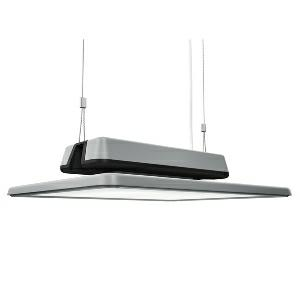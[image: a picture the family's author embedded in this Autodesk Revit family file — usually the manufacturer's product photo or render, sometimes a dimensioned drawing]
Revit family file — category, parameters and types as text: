
# Revit family: acaneo_-_hial_20000_840_w_dali_00734216_865c
name_source: partatom
category: Lighting Fixtures
units: mm (PartAtom-declared; Revit-internal decimal feet)

## family parameters
Cut with Voids When Loaded = No
Host = Face
Light Source = No
Part Type = Normal
Room Calculation Point = No
Round Connector Dimension = Use Diameter
Shared = No

## types (1)
- ACANEO - HIAL 20000/840/W/DALI (1 x LED, 22000 lm, 4000K)
    Apparent Load = 140 VA
    Approval mark = CE
    CIE Flux Codes = 76 97 99 100 100
    Color Rendering = 80-89
    Color Temperature = 4000K
    Control Gear = Electronic ballast
    Default Elevation = 1800 mm
    Description = HIAL 20000/840/W/DALI|High bay luminaire|light source: LED|work equipment: Adjustable electronic ballast, digital DALI|connected load: 220-240 V, 50/60 Hz|Power consumption: approx. 140 W|power factor: approx. 0,951|luminous flux: 22000 lm|luminous efficacy: 157 lm/W|colour temperature: Cold white, ca. 4000 K|color rendering index (CRI): >= 80|chromaticity tolerance:  3 SDCM|System of protection: IP 65|class of protection: I|technology: Continuously dimmable|luminaire body|material: Aluminium|surface: Powder coatet|colour: White aluminium|lamp cover: Acrylic (PMMA), Clear|weight (net): approx. 8.2 kg|mains lead: Built-in plug RST 20i5 Einbau|Fastening: Available separately|Accessory: Junction box (RST 20i5)|minimum ambient temperature: -30 ░C|maximum ambient temperature: 70 ░C|glare control: Optics|unified glare rating(4H 8H): <=  25|
    Frequency = 50 Hz, 60 Hz
    Height = 125 mm
    Lamp = 1 x LED
    Lamp Light Flux = 22000 lm
    Lamp count = 1
    Length = 480 mm
    Luminous efficacy = 157 lm/W
    Manufacturer = Waldmann
    ModVariant = No
    Model = 00734216
    Mounting Place = Ceiling
    Mounting Type = Pendant
    Number of Poles = 1
    OnlyDefault = Yes
    Power Factor = 1
    Product Name = ACANEO - HIAL 20000/840/W/DALI
    Product group = High bay luminaire (industry)
    ProductGroupID = 901
    Protection Class = Protection class I
    Protection Degree = IP 65
    RLX_Detail_Level = 1
    RLX_Emergency_Light_Flux = 0 lm
    RLX_Emergency_Type = 0
    RLX_Emergency_Type_DB = No
    RlxData = <blob elided: 31325 chars, md5=4be07580>
    Socket = socket
    Standby Power = 0 W
    System Light Flux = 22000 lm
    System Power = 140 W
    Type Comments = Product without accessories
    Type Image = acaneo-hial.jpg
    URL = http://relux.com
    VarID = ---
    Voltage = 230 V
    Voltage Range = 110-120 V, 220-240 V
    Weight = 0.00 kg
    Width = 405 mm

## geometry (parser evidence)
native form markers: Blend x4, Sweep x8
no freeform markers — native parametric forms only
